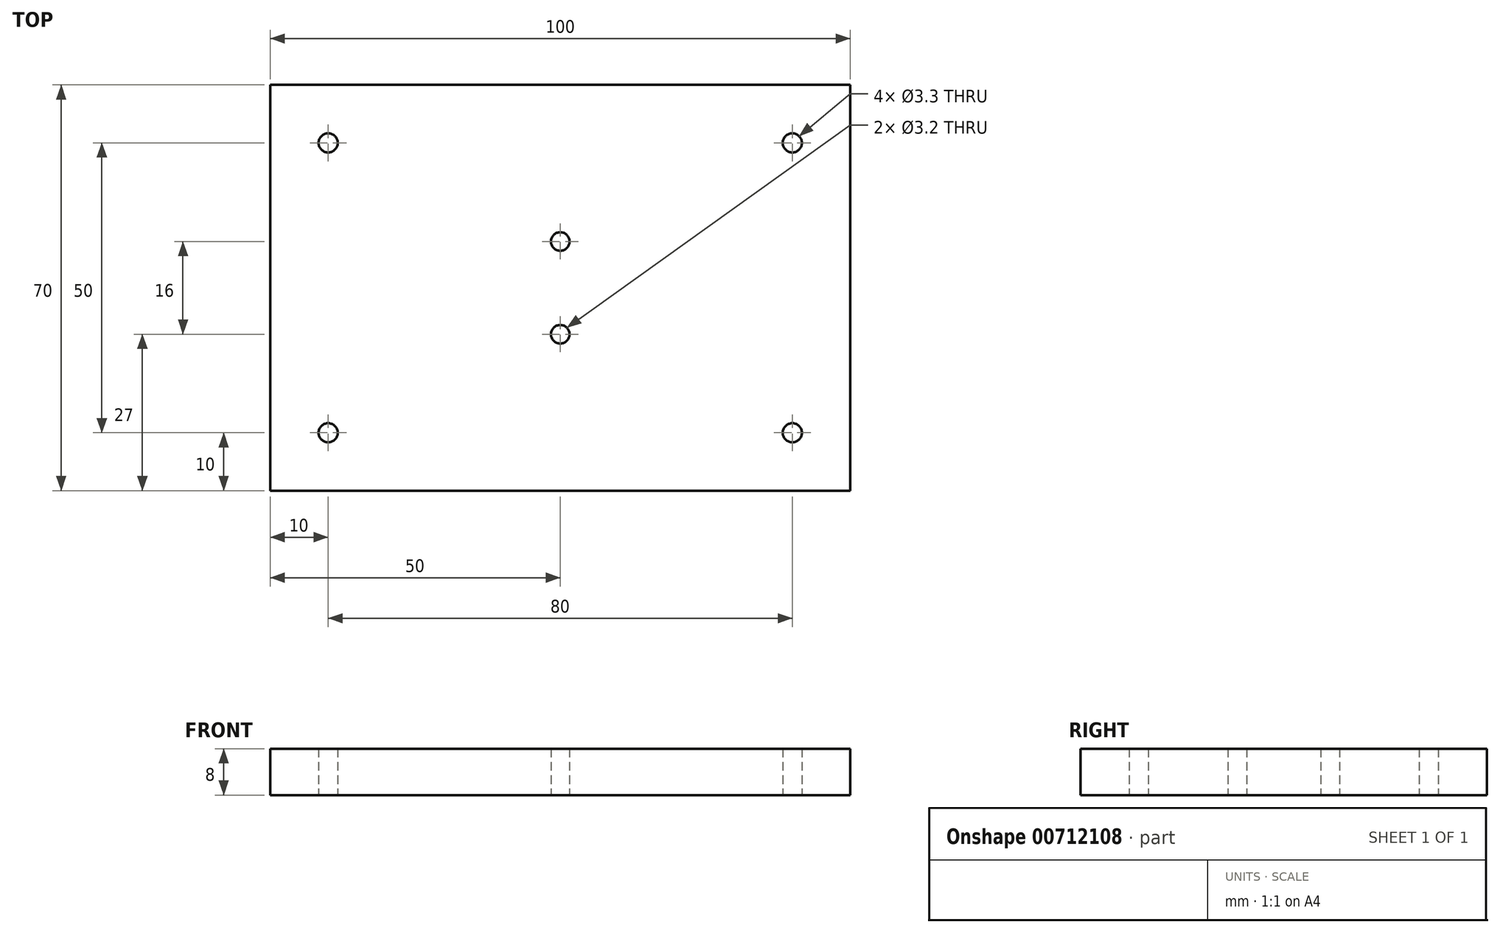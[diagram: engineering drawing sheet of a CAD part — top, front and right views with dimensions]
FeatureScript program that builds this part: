
annotation { "Feature Type Name" : "Feature", "Feature Type Description" : "" }
export const myFeature = defineFeature(function(context is Context, id is Id, definition is map)
    precondition{}
    {
        {
            var Q0;
            Q0=qCreatedBy(makeId("Top.planeOp"),FACE);
            var sketch = newSketch(context, id + "F0", { "sketchPlane" : qUnion([Q0])});
            skLineSegment(sketch, "E0.bottom", {"start": v(-50, 35) * mm, "end": v(50, 35) * mm});
            skLineSegment(sketch, "E0.top", {"start": v(-50, -35) * mm, "end": v(50, -35) * mm});
            skLineSegment(sketch, "E0.left", {"start": v(-50, 35) * mm, "end": v(-50, -35) * mm});
            skLineSegment(sketch, "E0.right", {"start": v(50, 35) * mm, "end": v(50, -35) * mm});
            skPoint(sketch, "E0.middle", {"position": v(0, 0) * mm});
            skSolve(sketch);
        }
        {
            var Q0;
            Q0=makeQuery(id+"F0.imprint","IMPRINT",FACE,{"disambiguationData":[TD([[makeQuery(id+"F0.imprint","IMPRINT",EDGE,{"derivedFrom":sQuery(id+"F0.wireOp",EDGE,"E0.bottom")}),-1.0]])]});
            extrude(context, id + "F1", {"entities" : qUnion([Q0]), "depth" : 8 * mm, "offsetDistance" : 25 * mm, "symmetric" : true});
        }
        {
            var Q0;
            Q0=makeQuery(id+"F1.opExtrude","CAP_FACE",FACE,{"disambiguationData":[OSD([sQuery(id+"F0.wireOp",EDGE,"E0.bottom"),sQuery(id+"F0.wireOp",EDGE,"E0.top"),sQuery(id+"F0.wireOp",EDGE,"E0.left"),sQuery(id+"F0.wireOp",EDGE,"E0.right")])],"isStart":false});
            var sketch = newSketch(context, id + "F2", { "sketchPlane" : qUnion([Q0])});
            skLineSegment(sketch, "E1.0", {"start": v(-50, 25) * mm, "end": v(50, 25) * mm, "construction": true});
            skLineSegment(sketch, "E2.0", {"start": v(-50, 8) * mm, "end": v(50, 8) * mm, "construction": true});
            skLineSegment(sketch, "E3.0", {"start": v(-40, 35) * mm, "end": v(-40, -35) * mm, "construction": true});
            skLineSegment(sketch, "E4.MirrorCS", {"start": v(40, 35) * mm, "end": v(40, -35) * mm, "construction": true});
            skLineSegment(sketch, "E5.MirrorCS", {"start": v(-50, -8) * mm, "end": v(50, -8) * mm, "construction": true});
            skLineSegment(sketch, "E6.MirrorCS", {"start": v(-50, -25) * mm, "end": v(50, -25) * mm, "construction": true});
            skPoint(sketch, "E7", {"position": v(-40, 25) * mm});
            skPoint(sketch, "E8", {"position": v(40, 25) * mm});
            skPoint(sketch, "E9", {"position": v(40, -25) * mm});
            skPoint(sketch, "E10", {"position": v(-40, -25) * mm});
            skPoint(sketch, "E11", {"position": v(0, 8) * mm});
            skPoint(sketch, "E12", {"position": v(0, -8) * mm});
            skSolve(sketch);
        }
        {
            var Q0;
            Q0=sQuery(id+"F2.wireOp",VERTEX,"E8");
            var Q1;
            Q1=sQuery(id+"F2.wireOp",VERTEX,"E9");
            var Q2;
            Q2=sQuery(id+"F2.wireOp",VERTEX,"E10");
            var Q3;
            Q3=sQuery(id+"F2.wireOp",VERTEX,"E7");
            var Q4;
            Q4=makeQuery(id+"F1.opExtrude","SWEPT_BODY",BODY,{"disambiguationData":[OSD([sQuery(id+"F0.wireOp",EDGE,"E0.bottom"),sQuery(id+"F0.wireOp",EDGE,"E0.top"),sQuery(id+"F0.wireOp",EDGE,"E0.left"),sQuery(id+"F0.wireOp",EDGE,"E0.right")])]});
            hole(context, id + "F3", {"style" : HoleStyle.SIMPLE, "endStyle" : HoleEndStyle.THROUGH, "standardTappedOrClearance" : lookupTablePath({ "standard" : "ISO", "fit" : "Normal", "size" : "M3", "type" : "Clearance" }), "standardBlindInLast" : lookupTablePath({ "fit" : "Standard", "standard" : "ISO", "size" : "M3", "type" : "Clearance" }), "holeDiameter" : 3.3 * mm, "majorDiameter" : 5 * mm, "tappedDepth" : 12 * mm, "tapClearance" : 3, "locations" : qUnion([Q0, Q1, Q2, Q3]), "scope" : qUnion([Q4]), "startStyle" : HoleStartStyle.PART});
        }
        {
            var Q0;
            Q0=sQuery(id+"F2.wireOp",VERTEX,"E11");
            var Q1;
            Q1=sQuery(id+"F2.wireOp",VERTEX,"E12");
            var Q2;
            Q2=makeQuery(id+"F1.opExtrude","SWEPT_BODY",BODY,{"disambiguationData":[OSD([sQuery(id+"F0.wireOp",EDGE,"E0.bottom"),sQuery(id+"F0.wireOp",EDGE,"E0.top"),sQuery(id+"F0.wireOp",EDGE,"E0.left"),sQuery(id+"F0.wireOp",EDGE,"E0.right")])]});
            hole(context, id + "F4", {"style" : HoleStyle.SIMPLE, "endStyle" : HoleEndStyle.THROUGH, "holeDiameter" : 3.2 * mm, "majorDiameter" : 5 * mm, "tappedDepth" : 12 * mm, "tapClearance" : 3, "locations" : qUnion([Q0, Q1]), "scope" : qUnion([Q2]), "startStyle" : HoleStartStyle.PART});
        }
    });
